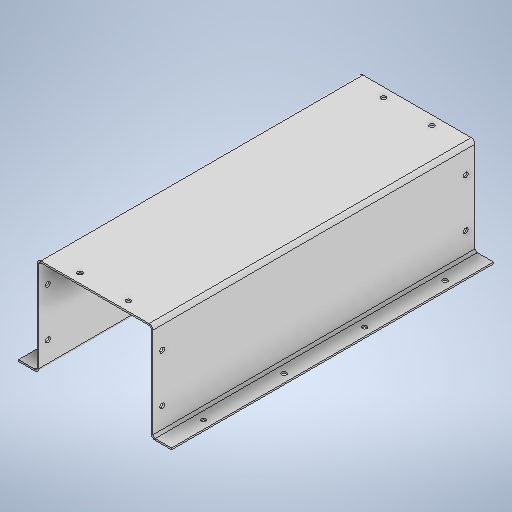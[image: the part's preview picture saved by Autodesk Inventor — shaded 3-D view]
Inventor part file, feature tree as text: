
AUTODESK INVENTOR PART (.ipt)
format: ipt  version: 2025 (Build 290162010, 162A)  size: 394,752 bytes
history: native  units: mm
features: sheet_metal_op x13, sketch x8, other x6, extrude x3, pattern_linear x1, mirror x1
ambient origin geometry x8: Origin, YZ Plane, XZ Plane, XY Plane, X Axis, Y Axis, Z Axis, Center Point
bodies: Solid1 (feature_tree)
feature tree (32):
  sheet_metal_op  "Face1"
  sheet_metal_op  "Flange1"
  sheet_metal_op  "Flange2"
  sheet_metal_op  "Flange3"
  sheet_metal_op  "Flange4"
  extrude  "Extrusion1"  Depth=400.0mm
  pattern_linear  "Rectangular Pattern2"  Count1=12  [1 undecoded]
  extrude  "Extrusion3"  Depth=2.75mm
  extrude  "Extrusion4"  Depth=2.75mm
  mirror  "Mirror2"
  sketch  "Sketch1"  dims[d0=140.0mm d1=400.0mm]
  other  "Plate1"
  sketch  "Sketch2"  dims[d2=2.0mm]
  other  "Plate2"
  sheet_metal_op  "Bend1"
  sheet_metal_op  "Corner1"
  sketch  "Sketch3"  dims[d3=2.0mm]
  other  "Plate3"
  sheet_metal_op  "Bend2"
  sheet_metal_op  "Corner2"
  sketch  "Sketch4"  dims[d4=1.0mm]
  other  "Plate4"
  sheet_metal_op  "Bend3"
  sheet_metal_op  "Corner3"
  sketch  "Sketch5"  dims[d5=4.0mm]
  other  "Plate5"
  sheet_metal_op  "Bend4"
  sheet_metal_op  "Corner4"
  sketch  "Sketch6"  dims[d6=2.75mm d7=120.0mm]
  sketch  "Sketch8"  dims[d8=90.0deg d9=2.75mm d10=8.0mm]
  sketch  "Sketch9"  dims[d11=2.0mm d12=2.75mm d13=2.0mm d14=1.0mm d15=4.0mm d16=2.75mm d17=120.0mm d18=90.0deg d19=2.75mm d20=8.0mm d21=2.0mm d22=2.75mm d23=2.0mm d24=1.0mm d25=4.0mm d26=2.75mm d27=25.0mm d28=90.0deg d29=2.75mm d30=8.0mm d31=2.0mm d32=2.75mm d33=2.0mm d34=1.0mm d35=4.0mm d36=2.75mm d37=25.0mm d38=90.0deg d39=2.75mm d40=8.0mm d41=2.0mm d42=2.75mm d43=6.0mm d44=50.0mm d45=0.0mm d46=0.0mm d60=40.0mm d62=100.0mm d63=20.0mm d65=169.75mm d68=6.0mm d69=60.0mm d70=0.0mm d71=0.0mm d72=6.0mm d73=11.5mm d74=37.3mm d76=0.0mm d77=0.0mm d78=30.0mm d79=11.5mm d80=60.0mm]
  other  "Definition1"
note: 1 required parameter value undecoded (feature->parameter linkage not recoverable at this tier; creation-order binding heuristic only, values carry confidence <= 0.55)
